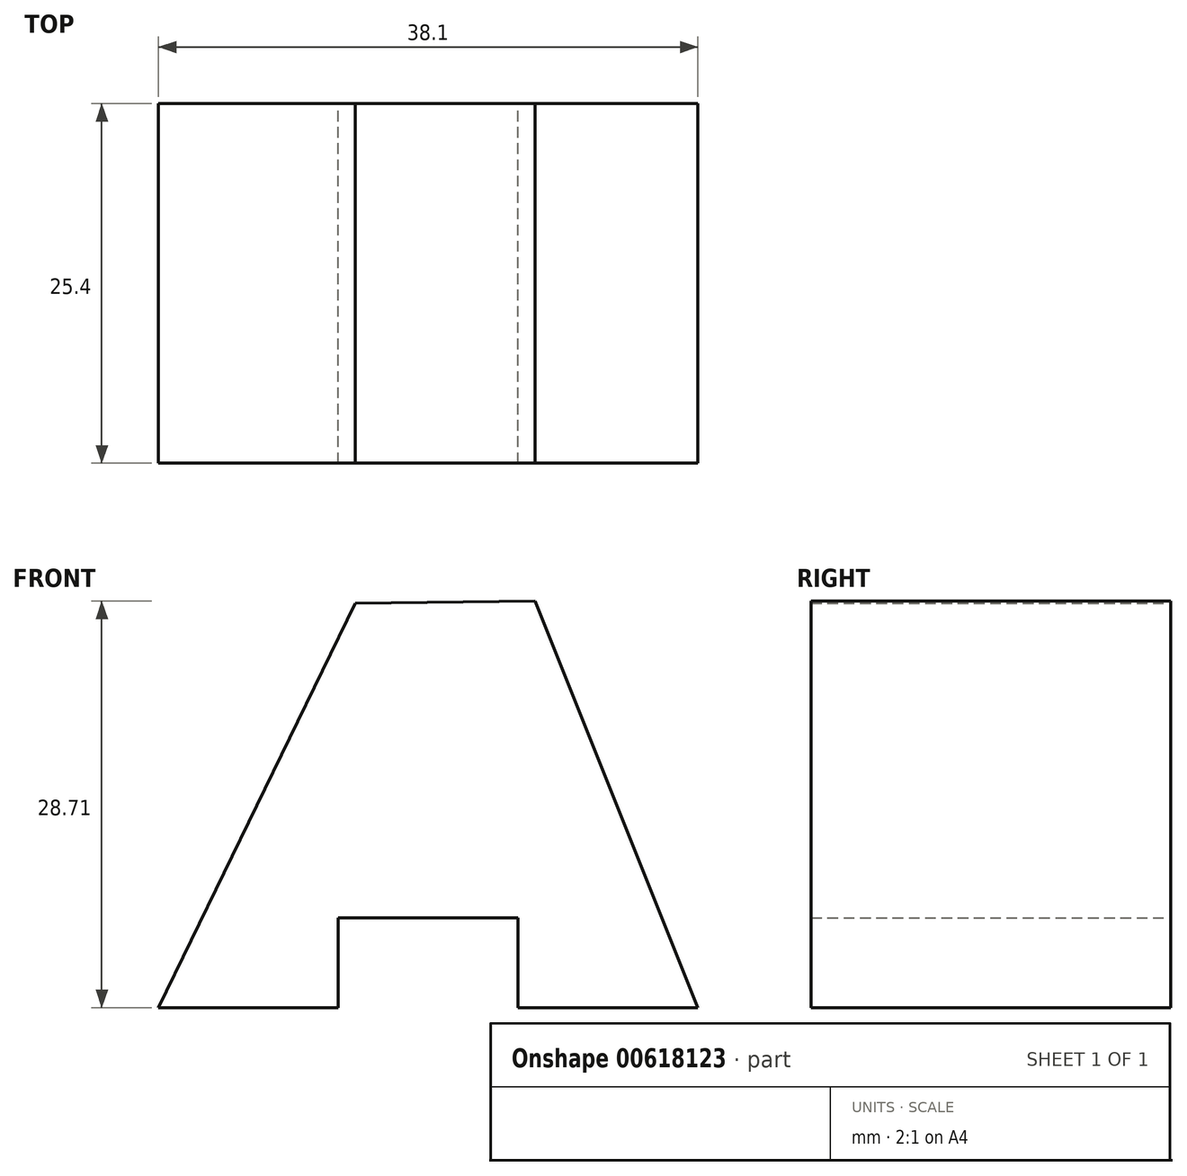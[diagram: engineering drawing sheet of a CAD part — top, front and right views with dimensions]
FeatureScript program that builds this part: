
annotation { "Feature Type Name" : "Feature", "Feature Type Description" : "" }
export const myFeature = defineFeature(function(context is Context, id is Id, definition is map)
    precondition{}
    {
        {
            var Q0;
            Q0=qCreatedBy(makeId("Front.planeOp"),FACE);
            var sketch = newSketch(context, id + "F0", { "sketchPlane" : qUnion([Q0])});
            skLineSegment(sketch, "E0", {"start": v(0, 0) * mm, "end": v(13.9, 28.55) * mm});
            skLineSegment(sketch, "E1", {"start": v(13.9, 28.55) * mm, "end": v(26.6, 28.7) * mm});
            skLineSegment(sketch, "E2", {"start": v(26.6, 28.7) * mm, "end": v(38.1, 0) * mm});
            skLineSegment(sketch, "E3", {"start": v(38.1, 0) * mm, "end": v(25.4, 0) * mm});
            skLineSegment(sketch, "E4", {"start": v(25.4, 0) * mm, "end": v(25.4, 6.35) * mm});
            skLineSegment(sketch, "E5", {"start": v(25.4, 6.35) * mm, "end": v(12.7, 6.35) * mm});
            skLineSegment(sketch, "E6", {"start": v(12.7, 6.35) * mm, "end": v(12.7, 0) * mm});
            skLineSegment(sketch, "E7", {"start": v(12.7, 0) * mm, "end": v(0, 0) * mm});
            skSolve(sketch);
        }
        {
            var Q0;
            Q0=makeQuery(id+"F0.imprint","IMPRINT",FACE,{"disambiguationData":[TD([[makeQuery(id+"F0.imprint","IMPRINT",EDGE,{"derivedFrom":sQuery(id+"F0.wireOp",EDGE,"E0")}),-1.0]])]});
            extrude(context, id + "F1", {"entities" : qUnion([Q0]), "depth" : 25.4 * mm, "offsetDistance" : 25.4 * mm});
        }
    });
